# Revit family: ВУТ ПБ
name_source: partatom
category: Mechanical Equipment
units: mm (PartAtom-declared; Revit-internal decimal feet)

## family parameters
Always vertical = Yes
Classification = None
Cut with Voids When Loaded = No
Part Type = Normal
Room Calculation Point = No
Round Connector Dimension = Use Diameter
Shared = No
Work Plane-Based = No

## types (8) — shared parameters
00_20_Виробник = Вентс
00_20_Назва = Припливно-витяжна установка
Manufacturer = Вентс
URL = https://vents.ua
l = 50 mm  [stored 0.164042 ft]
Клас фільтрації = G4, F7
Класифікація навантаження = HVAC
Кількість фаз = 1
Матеріал зони обслуговуваня = <By Category>
Напруга = 230 V
Частота = 50 Hz
zero-valued in all types: Default Elevation

## per-type parameters (varying)
- ВУТ 160 ПБ ЕС Л А21: -h=-160 mm  [stored -0.524934 ft]; A=500 mm  [stored 1.64042 ft]; Alfa=180.00°; B=754 mm  [stored 2.47375 ft]; D=125 mm  [stored 0.410105 ft]; Dy=120 mm  [stored 0.393701 ft]; H=320 mm  [stored 1.04987 ft]; He=160 mm  [stored 0.524934 ft]; L=1008 mm  [stored 3.30709 ft]; Le=397 mm; h1=20 mm  [stored 0.0656168 ft]; l2=245 mm  [stored 0.803806 ft]; l22=144 mm  [stored 0.472441 ft]; l222=245 mm  [stored 0.803806 ft]; l3=159 mm  [stored 0.521654 ft]; l4=128 mm  [stored 0.419948 ft]; l5=123 mm  [stored 0.403543 ft]; l6=216 mm  [stored 0.708661 ft]; Вага=48.00 kg; Верхнее крепление=Yes; Висота=320 mm  [stored 1.04987 ft]; Довжина=1108 mm  [stored 3.63517 ft]; Діаметр=125 mm  [stored 0.410105 ft]; Левое=Yes; Максимальний потік повітря=190.0 m³/h; Матеріал корпусу=Сталь, гальванізована; Потужність=50 W; Правое=No; Рівень звукового тиску на відстані 3 м=26 дБА; Струм=0 A; Тип 180=No; Установлена потужність=92 VA; Ширина=839 mm  [stored 2.75262 ft]
- ВУТ 160 ПБ ЕС П А21: -h=-160 mm  [stored -0.524934 ft]; A=500 mm  [stored 1.64042 ft]; Alfa=0.00°; B=754 mm  [stored 2.47375 ft]; D=125 mm  [stored 0.410105 ft]; Dy=120 mm  [stored 0.393701 ft]; H=320 mm  [stored 1.04987 ft]; He=160 mm  [stored 0.524934 ft]; L=1008 mm  [stored 3.30709 ft]; Le=397 mm; h1=20 mm  [stored 0.0656168 ft]; l2=123 mm  [stored 0.403543 ft]; l22=216 mm  [stored 0.708661 ft]; l222=216 mm  [stored 0.708661 ft]; l3=128 mm  [stored 0.419948 ft]; l4=159 mm  [stored 0.521654 ft]; l5=245 mm  [stored 0.803806 ft]; l6=245 mm  [stored 0.803806 ft]; Вага=48.00 kg; Верхнее крепление=Yes; Висота=320 mm  [stored 1.04987 ft]; Довжина=1108 mm  [stored 3.63517 ft]; Діаметр=125 mm  [stored 0.410105 ft]; Левое=No; Максимальний потік повітря=190.0 m³/h; Матеріал корпусу=Сталь, гальванізована; Потужність=50 W; Правое=Yes; Рівень звукового тиску на відстані 3 м=26 дБА; Струм=0 A; Тип 180=No; Установлена потужність=92 VA; Ширина=839 mm  [stored 2.75262 ft]
- ВУТ 250 ПБ ЕС П А21: -h=-160 mm  [stored -0.524934 ft]; A=500 mm  [stored 1.64042 ft]; Alfa=0.00°; B=754 mm  [stored 2.47375 ft]; D=125 mm  [stored 0.410105 ft]; Dy=120 mm  [stored 0.393701 ft]; H=320 mm  [stored 1.04987 ft]; He=160 mm  [stored 0.524934 ft]; L=1008 mm  [stored 3.30709 ft]; Le=397 mm; h1=20 mm  [stored 0.0656168 ft]; l2=123 mm  [stored 0.403543 ft]; l22=216 mm  [stored 0.708661 ft]; l222=216 mm  [stored 0.708661 ft]; l3=128 mm  [stored 0.419948 ft]; l4=159 mm  [stored 0.521654 ft]; l5=245 mm  [stored 0.803806 ft]; l6=245 mm  [stored 0.803806 ft]; Вага=48.00 kg; Верхнее крепление=Yes; Висота=320 mm  [stored 1.04987 ft]; Довжина=1108 mm  [stored 3.63517 ft]; Діаметр=125 mm  [stored 0.410105 ft]; Левое=No; Максимальний потік повітря=270.0 m³/h; Матеріал корпусу=Сталь, гальванізована; Потужність=101 W; Правое=Yes; Рівень звукового тиску на відстані 3 м=28 дБА; Струм=1 A; Тип 180=No; Установлена потужність=184 VA; Ширина=839 mm  [stored 2.75262 ft]
- ВУТ 250 ПБ ЕС Л А21: -h=-160 mm  [stored -0.524934 ft]; A=500 mm  [stored 1.64042 ft]; Alfa=180.00°; B=754 mm  [stored 2.47375 ft]; D=125 mm  [stored 0.410105 ft]; Dy=120 mm  [stored 0.393701 ft]; H=320 mm  [stored 1.04987 ft]; He=160 mm  [stored 0.524934 ft]; L=1008 mm  [stored 3.30709 ft]; Le=397 mm; h1=20 mm  [stored 0.0656168 ft]; l2=245 mm  [stored 0.803806 ft]; l22=144 mm  [stored 0.472441 ft]; l222=245 mm  [stored 0.803806 ft]; l3=159 mm  [stored 0.521654 ft]; l4=128 mm  [stored 0.419948 ft]; l5=123 mm  [stored 0.403543 ft]; l6=216 mm  [stored 0.708661 ft]; Вага=48.00 kg; Верхнее крепление=Yes; Висота=320 mm  [stored 1.04987 ft]; Довжина=1108 mm  [stored 3.63517 ft]; Діаметр=125 mm  [stored 0.410105 ft]; Левое=Yes; Максимальний потік повітря=270.0 m³/h; Матеріал корпусу=Сталь, гальванізована; Потужність=101 W; Правое=No; Рівень звукового тиску на відстані 3 м=28 дБА; Струм=1 A; Тип 180=No; Установлена потужність=184 VA; Ширина=839 mm  [stored 2.75262 ft]
- ВУТ 350 ПБ ЕС Л А21: -h=-160 mm  [stored -0.524934 ft]; A=700 mm  [stored 2.29659 ft]; Alfa=180.00°; B=1044 mm; D=160 mm  [stored 0.524934 ft]; Dy=155 mm  [stored 0.50853 ft]; H=320 mm  [stored 1.04987 ft]; He=160 mm  [stored 0.524934 ft]; L=1138 mm  [stored 3.7336 ft]; Le=542 mm  [stored 1.77822 ft]; h1=20 mm  [stored 0.0656168 ft]; l2=345 mm  [stored 1.13189 ft]; l22=144 mm  [stored 0.472441 ft]; l222=345 mm  [stored 1.13189 ft]; l3=159 mm  [stored 0.521654 ft]; l4=119 mm  [stored 0.39042 ft]; l5=144 mm  [stored 0.472441 ft]; l6=282 mm; Вага=70.00 kg; Верхнее крепление=Yes; Висота=320 mm  [stored 1.04987 ft]; Довжина=1238 mm; Діаметр=160 mm  [stored 0.524934 ft]; Левое=Yes; Максимальний потік повітря=410.0 m³/h; Матеріал корпусу=Сталь, гальванізована; Потужність=170 W; Правое=No; Рівень звукового тиску на відстані 3 м=34 дБА; Струм=1 A; Тип 180=No; Установлена потужність=299 VA; Ширина=1129 mm  [stored 3.70407 ft]
- ВУТ 350 ПБ ЕС П А21: -h=-160 mm  [stored -0.524934 ft]; A=700 mm  [stored 2.29659 ft]; Alfa=0.00°; B=1044 mm; D=160 mm  [stored 0.524934 ft]; Dy=155 mm  [stored 0.50853 ft]; H=320 mm  [stored 1.04987 ft]; He=160 mm  [stored 0.524934 ft]; L=1138 mm  [stored 3.7336 ft]; Le=542 mm  [stored 1.77822 ft]; h1=20 mm  [stored 0.0656168 ft]; l2=144 mm  [stored 0.472441 ft]; l22=144 mm  [stored 0.472441 ft]; l222=144 mm  [stored 0.472441 ft]; l3=119 mm  [stored 0.39042 ft]; l4=159 mm  [stored 0.521654 ft]; l5=345 mm  [stored 1.13189 ft]; l6=345 mm  [stored 1.13189 ft]; Вага=70.00 kg; Верхнее крепление=Yes; Висота=320 mm  [stored 1.04987 ft]; Довжина=1238 mm; Діаметр=160 mm  [stored 0.524934 ft]; Левое=No; Максимальний потік повітря=410.0 m³/h; Матеріал корпусу=Сталь, гальванізована; Потужність=170 W; Правое=Yes; Рівень звукового тиску на відстані 3 м=34 дБА; Струм=1 A; Тип 180=No; Установлена потужність=299 VA; Ширина=1129 mm  [stored 3.70407 ft]
- ВУТ 180 П5Б ЕС А21: -h=-132 mm  [stored -0.433071 ft]; A=500 mm  [stored 1.64042 ft]; Alfa=0.00°; B=600 mm; D=150 mm  [stored 0.492126 ft]; Dy=145 mm  [stored 0.475722 ft]; H=264 mm  [stored 0.866142 ft]; He=215 mm  [stored 0.705381 ft]; L=900 mm  [stored 2.95276 ft]; Le=320 mm  [stored 1.04987 ft]; h1=0 mm  [stored 0 ft]; l2=137 mm  [stored 0.449475 ft]; l22=144 mm  [stored 0.472441 ft]; l222=137 mm  [stored 0.449475 ft]; l3=132 mm  [stored 0.433071 ft]; l4=132 mm  [stored 0.433071 ft]; l5=137 mm  [stored 0.449475 ft]; l6=137 mm  [stored 0.449475 ft]; Вага=14.00 kg; Верхнее крепление=No; Висота=264 mm  [stored 0.866142 ft]; Довжина=1000 mm  [stored 3.28084 ft]; Діаметр=150 mm  [stored 0.492126 ft]; Левое=No; Максимальний потік повітря=220.0 m³/h; Матеріал корпусу=Поліпропілен(чорний); Потужність=87 W; Правое=No; Рівень звукового тиску на відстані 3 м=33 дБА; Струм=1 A; Тип 180=Yes; Установлена потужність=163 VA; Ширина=620 mm  [stored 2.03412 ft]
- ВУЕ 180 П5Б ЕС А21: -h=-132 mm  [stored -0.433071 ft]; A=500 mm  [stored 1.64042 ft]; Alfa=0.00°; B=600 mm; D=150 mm  [stored 0.492126 ft]; Dy=145 mm  [stored 0.475722 ft]; H=264 mm  [stored 0.866142 ft]; He=215 mm  [stored 0.705381 ft]; L=900 mm  [stored 2.95276 ft]; Le=320 mm  [stored 1.04987 ft]; h1=0 mm  [stored 0 ft]; l2=137 mm  [stored 0.449475 ft]; l22=144 mm  [stored 0.472441 ft]; l222=137 mm  [stored 0.449475 ft]; l3=132 mm  [stored 0.433071 ft]; l4=132 mm  [stored 0.433071 ft]; l5=137 mm  [stored 0.449475 ft]; l6=137 mm  [stored 0.449475 ft]; Вага=14.00 kg; Верхнее крепление=No; Висота=264 mm  [stored 0.866142 ft]; Довжина=1000 mm  [stored 3.28084 ft]; Діаметр=150 mm  [stored 0.492126 ft]; Левое=No; Максимальний потік повітря=220.0 m³/h; Матеріал корпусу=Поліпропілен(чорний); Потужність=87 W; Правое=No; Рівень звукового тиску на відстані 3 м=33 дБА; Струм=1 A; Тип 180=Yes; Установлена потужність=163 VA; Ширина=620 mm  [stored 2.03412 ft]

note: column(s) folded — value = type name in every type: 00_20_Тип

note: [stored X ft] marks values corroborated as IEEE doubles in the binary element streams (Revit-internal decimal feet)
